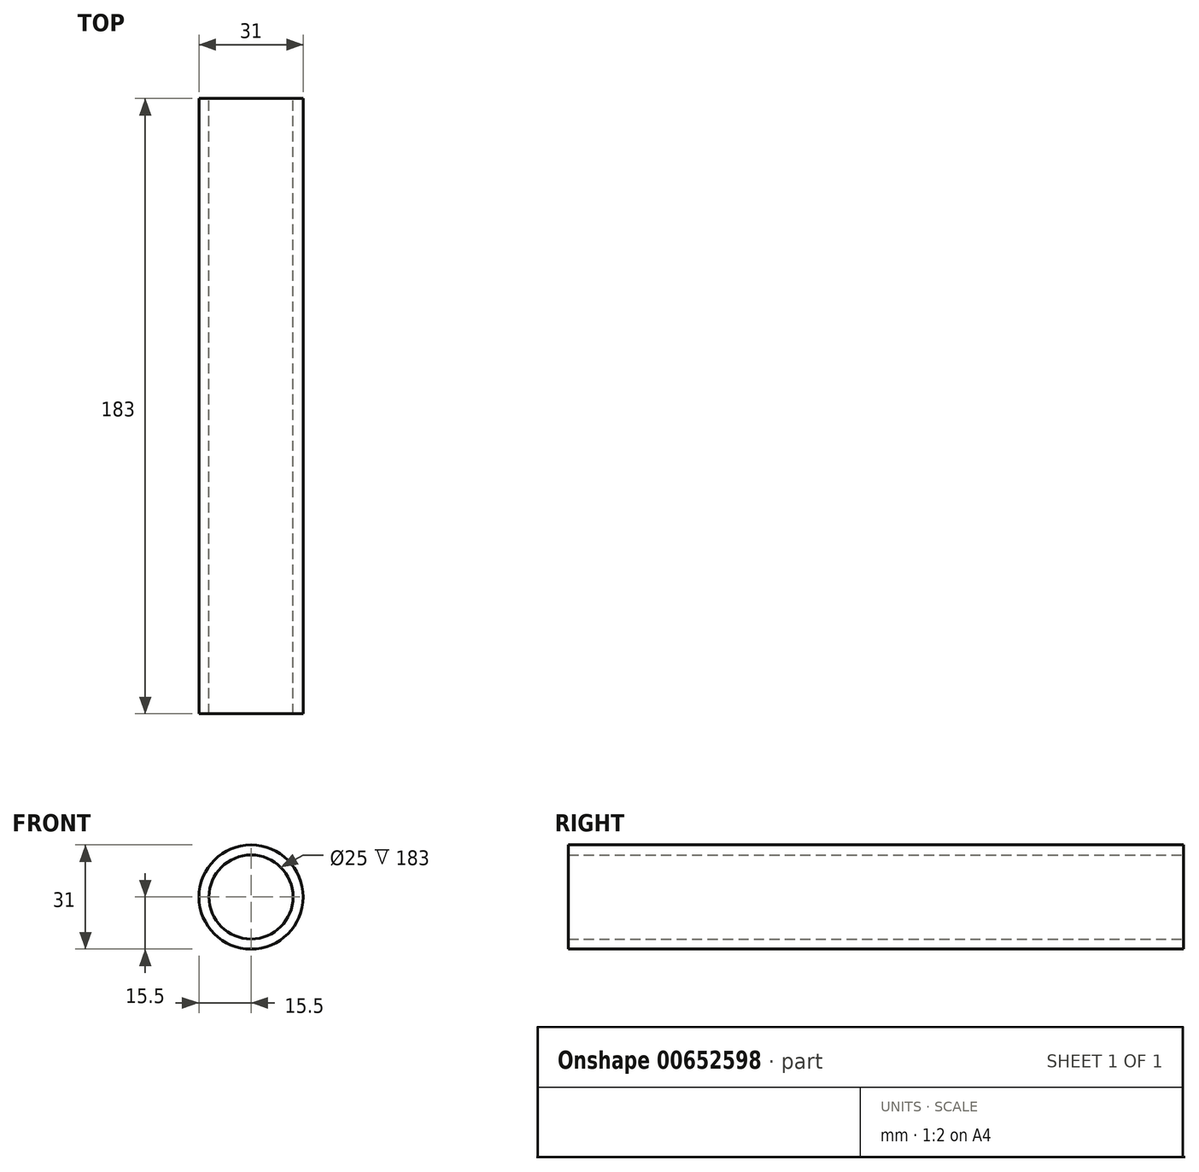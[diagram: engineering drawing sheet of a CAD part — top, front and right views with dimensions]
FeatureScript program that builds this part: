
annotation { "Feature Type Name" : "Feature", "Feature Type Description" : "" }
export const myFeature = defineFeature(function(context is Context, id is Id, definition is map)
    precondition{}
    {
        {
            var Q0;
            Q0=qCreatedBy(makeId("Front.planeOp"),FACE);
            var sketch = newSketch(context, id + "F0", { "sketchPlane" : qUnion([Q0])});
            skCircle(sketch, "E0", {"center": v(0, 0) * mm, "radius": 15.5 * mm});
            skCircle(sketch, "E1", {"center": v(0, 0) * mm, "radius": 12.5 * mm});
            skSolve(sketch);
        }
        {
            var Q0;
            Q0 = qSketchRegion(id + "F0", true);
            extrude(context, id + "F1", {"entities" : qUnion([Q0]), "depth" : (150 + 33) * mm, "offsetDistance" : 25 * mm});
        }
    });
